# Revit family: MaviGard Газовые извещатели серии
name_source: partatom
category: Fire Alarm Devices
units: mm (PartAtom-declared; Revit-internal decimal feet)

## family parameters
Cut with Voids When Loaded = No
Host = Face
Maintain Annotation Orientation = Yes
OmniClass Number = 23.85.30.21
OmniClass Title = Environmental Detection/Registration
Part Type = Normal
Room Calculation Point = No
Round Connector Dimension = Use Diameter
Shared = No

## types (13) — shared parameters
Manufacturer = Mavili Elektronik Ticaret A.Ş.
Model = MaviGard
URL = https://www.mavili.com.tr
Адрес №1 = Şerifali Mahallesi Kutup Sokak No:27/1-2-4 Ümraniye TR-34775 İSTANBUL
Вторичный материал = Пластмассовый
Гарантийный срок = Года
Гарантийный срок запчастей = 2
Гарантия срока службы = 2
Главный Материал = Белый пластмассовый PC/ABS
Инструкция по установке = https://mavilielektronik.com
Класс защиты = IP42
Монтажная поверхность = Настенная
Номер телефона = (+)90 216 466 45 05
Номер факса = (+)90 216 466 45 10
Номинальная высота = 100 мм
Номинальная глубина = 50 мм
Номинальная ширина = 140 мм
Производительность кода = EN 50194-1
Рабочая Температура = (-10°C) - (+55°C)
Совместимые базы для монтажа = ML-0120
Цвет = Белый
zero-valued in all types: Cost, Default Elevation

## per-type parameters (varying)
| type | Description | Диапазон рабочего напряжения | Код продукта | Монтажная высота | Настройка адреса устройства | Номер позы общественных работ | Рабочее напряжение (по умолчанию) | Резервное питание |
| MaviGardИзвещатель токсичной концентрации угарного газа, 24 В, 2 уров. тревоги, электрохимический | Извещатель токсичной концентрации угарного газа [CO] | 12-33В Пост. ток | GD2R-12EC | 150 см |  | 833-610 | 12 В Пост. ток | 24 В Пост. ток |
| MaviGard Извещатель токсичной концентрации угарного газа, 230 В, 2 уров. тревоги, электрохимический | Извещатель токсичной концентрации угарного газа [CO] | 18-33 В Пост. ток | GD2R-24EC | 150 см |  | 833-610 | 24 В Пост. ток | 24 В Пост. ток |
| MaviGard Неадресный извещатель токсичной концентрации угарного газа, 230 В, 2 уров. тревоги, электрохимический | Неадресный извещатель токсичной концентрации угарного газа [CO] | 18-33В Пост. ток | GD2R-220EC | 150 см |  | 833-610 | 24 В Пост. ток | 220 В Перем. ток |
| MaviGard серия GDR Неадресный извещатель сжиженного газа 12/24 В пост. ток, с реле | Неадресный извещатель сжиженного газа | 18-33В Пост. ток | GDR-1224L | 15-25 см |  | 833-606 | 24 В Пост. ток | 24 В Пост. ток |
| MaviGard серия GDR Неадресный извещатель сжиженного газа, 230 В перем. ток, с реле | Неадресный извещатель сжиженного газа | 18-33В Пост. ток | GDR-220L | 15-25 см |  | 833-606 | 24 В Пост. ток | 220 В Перем. ток |
| MaviGard серия GDR Неадресный извещатель природного газа, 12/24 В пост. ток, с реле | Неадресный извещатель природного газа | 12-33В Пост. ток | GDR-1224M | Ниже потолка на 5-15 см |  | 833-608 | 24 В Пост. ток | 24 В Пост. ток |
| MaviGard серия GDR Неадресный извещатель природного газа, 230 В перем. ток, с реле | Неадресный извещатель природного газа | 18-33В Пост. ток | GDR-220M | Ниже потолка на 5-15 см |  | 833-608 | 24 В Пост. ток | 220 В Перем. ток |
| MaviGard серия AGD Адресный извещатель токсичной концентрации угарного газа, 12/24 В пост. ток, электрохимический | Адресный извещатель токсичной концентрации угарного газа | 12-33В пост. ток | AGD-1224EC.VIP | 150 см | Модульная адресация |  | 24 В пост. ток | 24 В пост. ток |
| MaviGard Серия AGD Адресный извещатель токсичной концентрации угарного газа, 230 В перем. ток, электрохимический | Адресный извещатель токсичной концентрации угарного газа | 12-33В Пост. ток | AGD-220EC.VIP | 150 см | Модульная адресация |  | 24 В Пост. ток | 220 В Перем. ток |
| MaviGard серия  AGD Адресный извещатель утечки сжиженного газа, 12/24 В пост. ток | Адресный извещатель утечки сжиженного газа | 12-33В Пост. ток | AGD-1224L.VIP | 15-25 cм | Модульная адресация | 833-605 | 24 В Пост. ток | 24 В Пост. ток |
| MaviGard серия AGD Адресный извещатель утечки сжиженного газа, 230 В перем. ток | Адресный извещатель утечки сжиженного газа | 12-33В Пост. ток | AGD-220L.VIP | 15-25 см | Модульная адресация |  | 24В Пост. ток | 220В Перем. ток |
| MaviGard серия AGD Адресный извещатель утечки природного газа,12/24 В пост. ток | Адресный извещатель утечки природного газа | 12-33В Пост. ток | AGD-1224M.VIP | Ниже потолка на 5-15 см | Модульная адресация | 833-607 | 24 В Пост. ток | 24 В Пост. ток |
| MaviGard серия AGD Адресный извещатель утечки природного газа, 230 В перем. ток | Адресный извещатель утечки природного газа | 12-33В Пост. ток | AGD-220M.VIP | Ниже потолка на 5-15 см | Модульная адресация |  | 24 В Пост. ток | 220 В Перем. ток |

## geometry (parser evidence)
native form markers: Sweep x1
no freeform markers — native parametric forms only
